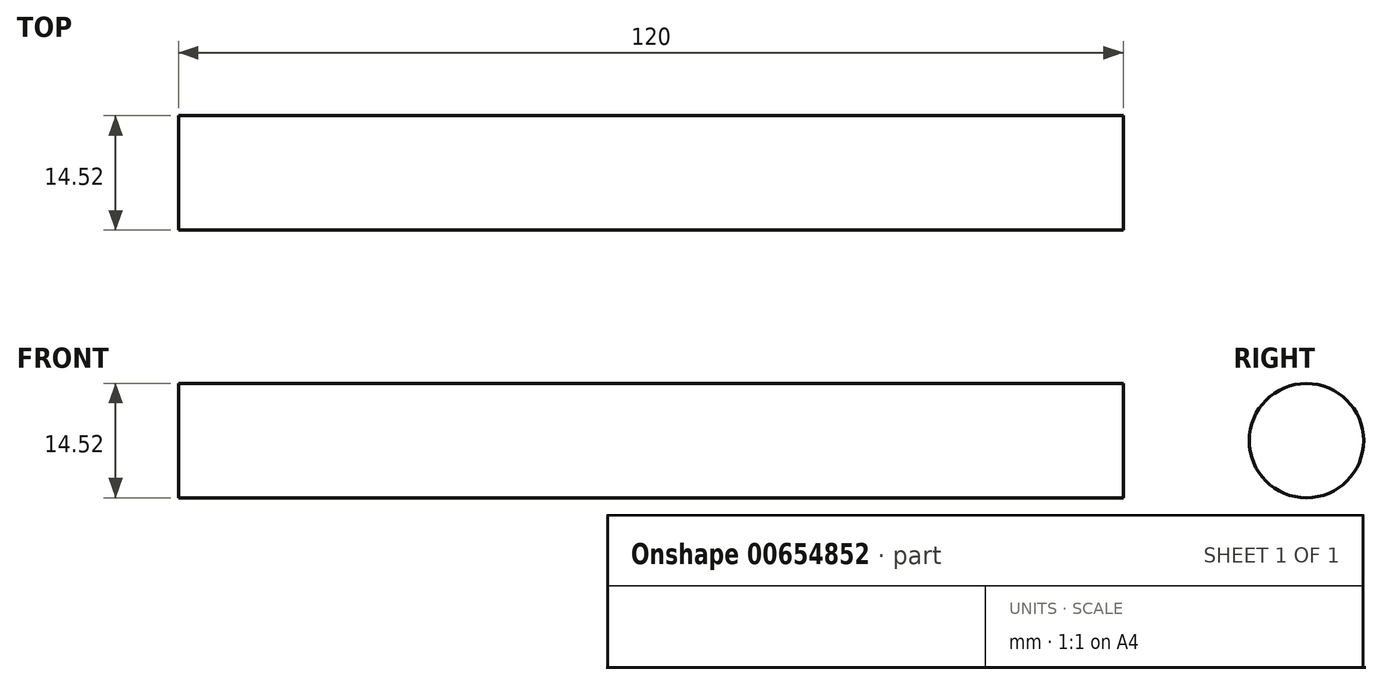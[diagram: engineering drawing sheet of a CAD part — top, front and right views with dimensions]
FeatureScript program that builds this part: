
annotation { "Feature Type Name" : "Feature", "Feature Type Description" : "" }
export const myFeature = defineFeature(function(context is Context, id is Id, definition is map)
    precondition{}
    {
        {
            var Q0;
            Q0=qCreatedBy(makeId("Right.planeOp"),FACE);
            var sketch = newSketch(context, id + "F0", { "sketchPlane" : qUnion([Q0])});
            skCircle(sketch, "E0", {"center": v(0, 0) * mm, "radius": 7.26 * mm});
            skSolve(sketch);
        }
        {
            var Q0;
            Q0=makeQuery(id+"F0.imprint","IMPRINT",FACE,{"disambiguationData":[TD([[makeQuery(id+"F0.imprint","IMPRINT",EDGE,{"derivedFrom":sQuery(id+"F0.wireOp",EDGE,"E0")}),1.0]])]});
            extrude(context, id + "F1", {"entities" : qUnion([Q0]), "depth" : 120 * mm, "offsetDistance" : 25.4 * mm});
        }
    });
